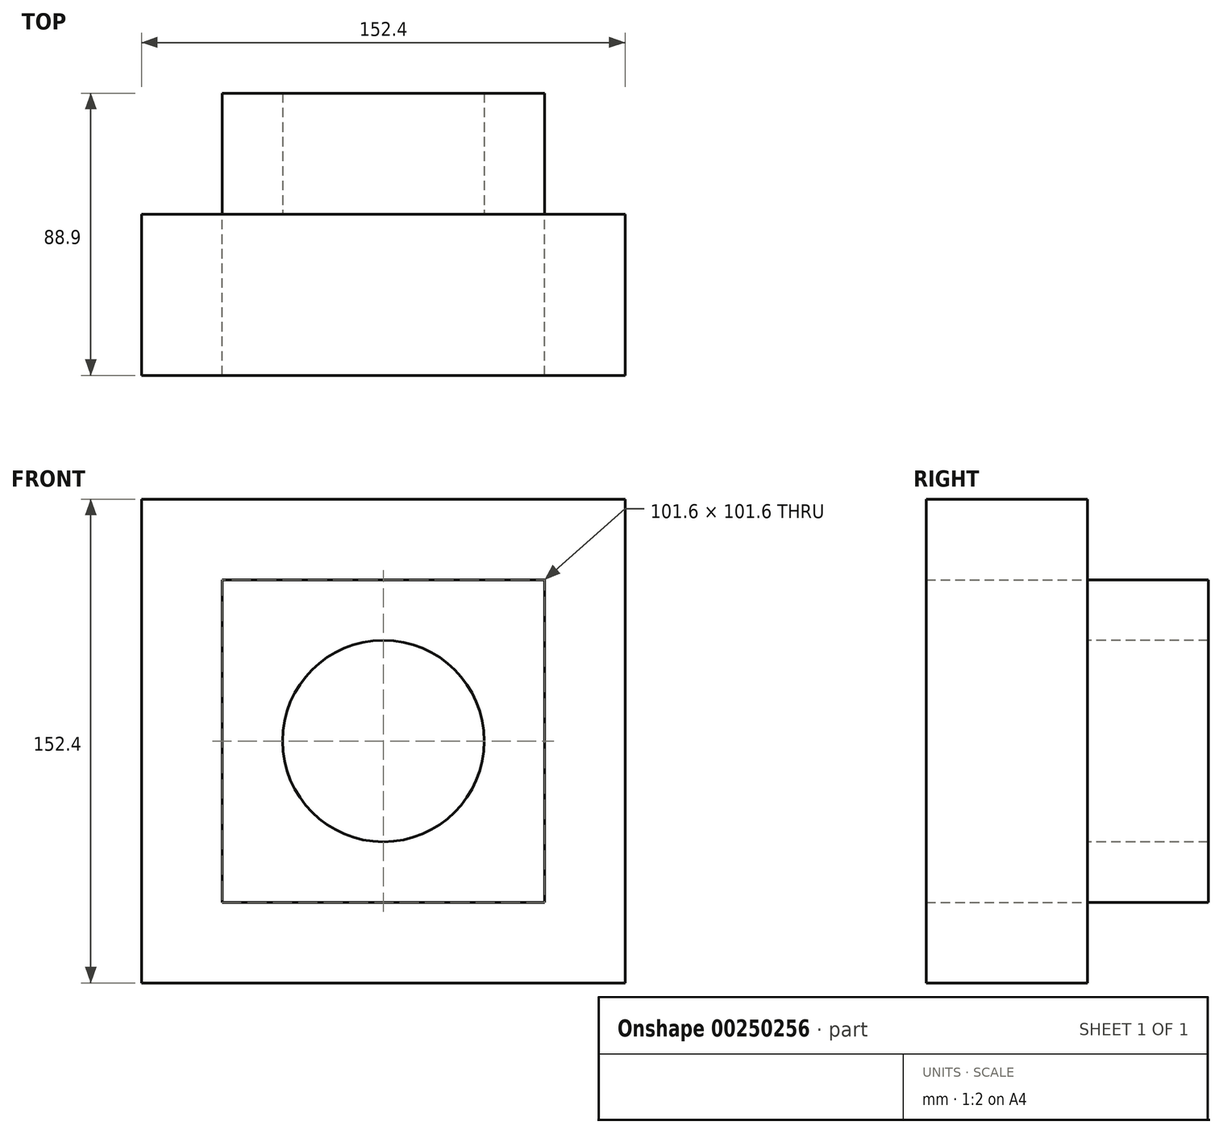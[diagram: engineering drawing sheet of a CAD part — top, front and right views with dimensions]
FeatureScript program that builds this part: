
annotation { "Feature Type Name" : "Feature", "Feature Type Description" : "" }
export const myFeature = defineFeature(function(context is Context, id is Id, definition is map)
    precondition{}
    {
        {
            var Q0;
            Q0=qCreatedBy(makeId("Front.planeOp"),FACE);
            var sketch = newSketch(context, id + "F0", { "sketchPlane" : qUnion([Q0])});
            skCircle(sketch, "E0", {"center": v(0, 0) * mm, "radius": 31.75 * mm});
            skLineSegment(sketch, "E1.bottom", {"start": v(-50.8, 50.8) * mm, "end": v(50.8, 50.8) * mm});
            skLineSegment(sketch, "E1.top", {"start": v(-50.8, -50.8) * mm, "end": v(50.8, -50.8) * mm});
            skLineSegment(sketch, "E1.left", {"start": v(-50.8, 50.8) * mm, "end": v(-50.8, -50.8) * mm});
            skLineSegment(sketch, "E1.right", {"start": v(50.8, 50.8) * mm, "end": v(50.8, -50.8) * mm});
            skLineSegment(sketch, "E2.bottom", {"start": v(-76.2, 76.2) * mm, "end": v(76.2, 76.2) * mm});
            skLineSegment(sketch, "E2.top", {"start": v(-76.2, -76.2) * mm, "end": v(76.2, -76.2) * mm});
            skLineSegment(sketch, "E2.left", {"start": v(-76.2, 76.2) * mm, "end": v(-76.2, -76.2) * mm});
            skLineSegment(sketch, "E2.right", {"start": v(76.2, 76.2) * mm, "end": v(76.2, -76.2) * mm});
            skSolve(sketch);
        }
        {
            var Q0;
            Q0=makeQuery(id+"F0.imprint","IMPRINT",FACE,{"disambiguationData":[TD([[makeQuery(id+"F0.imprint","IMPRINT",EDGE,{"derivedFrom":sQuery(id+"F0.wireOp",EDGE,"E0")}),-1.0]])]});
            extrude(context, id + "F1", {"entities" : qUnion([Q0]), "oppositeDirection" : true, "depth" : 38.1 * mm});
        }
        {
            var Q0;
            Q0=makeQuery(id+"F0.imprint","IMPRINT",FACE,{"disambiguationData":[TD([[makeQuery(id+"F0.imprint","IMPRINT",EDGE,{"derivedFrom":sQuery(id+"F0.wireOp",EDGE,"E1.bottom")}),1.0]])]});
            extrude(context, id + "F2", {"entities" : qUnion([Q0]), "operationType" : NewBodyOperationType.ADD, "depth" : 50.8 * mm});
        }
    });
